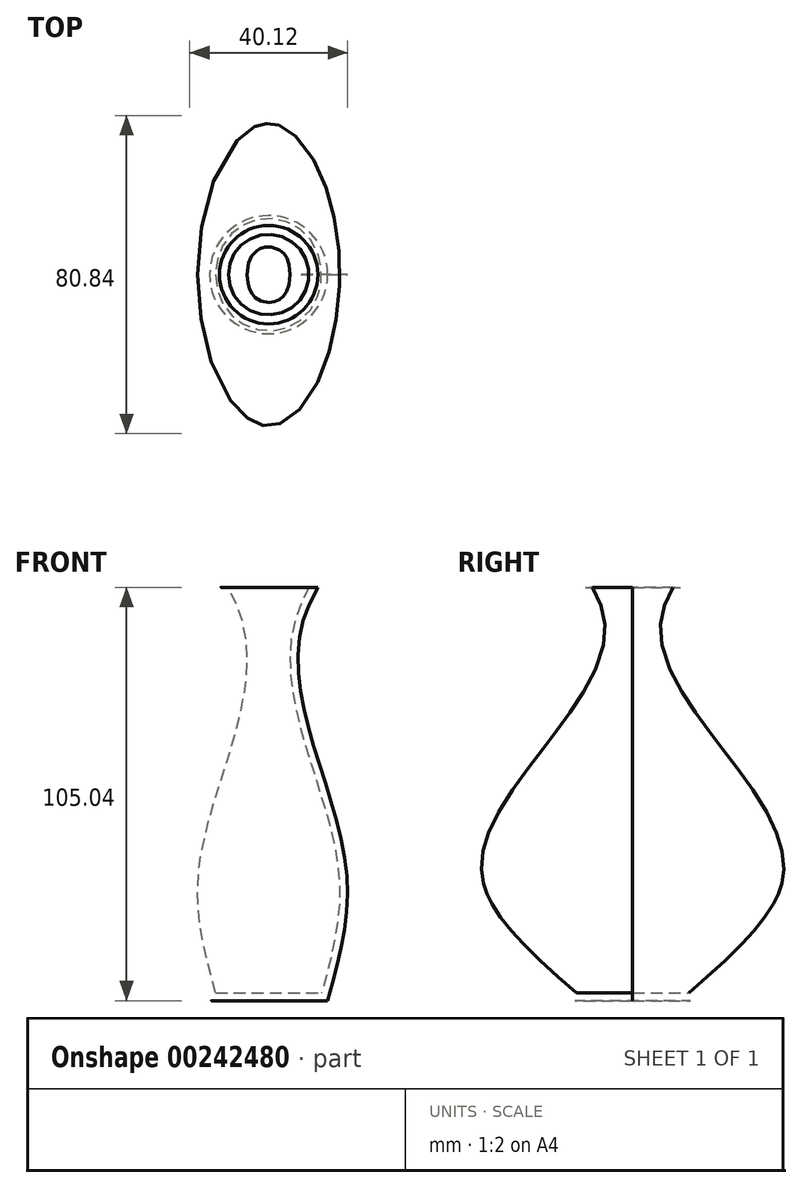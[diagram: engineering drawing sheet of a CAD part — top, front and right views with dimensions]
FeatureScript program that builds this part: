
annotation { "Feature Type Name" : "Feature", "Feature Type Description" : "" }
export const myFeature = defineFeature(function(context is Context, id is Id, definition is map)
    precondition{}
    {
        {
            var Q0;
            Q0=qCreatedBy(makeId("Top.planeOp"),FACE);
            var sketch = newSketch(context, id + "F0", { "sketchPlane" : qUnion([Q0])});
            skCircle(sketch, "E0", {"center": v(0, 0) * mm, "radius": 15 * mm});
            skSolve(sketch);
        }
        {
            var Q0;
            Q0=qCreatedBy(makeId("Top.planeOp"),FACE);
            cPlane(context, id + "F1", {"entities" : qUnion([Q0]), "cplaneType" : CPlaneType.OFFSET, "offset" : 30 * mm, "width" : 150 * mm, "height" : 150 * mm});
        }
        {
            var Q0;
            Q0=qCreatedBy(id+"F1.planeOp",FACE);
            var sketch = newSketch(context, id + "F2", { "sketchPlane" : qUnion([Q0])});
            skEllipse(sketch, "E1", {"center": v(0, 0) * mm, "majorRadius": 40 * mm, "minorRadius": 20 * mm, "majorAxis": v(0, -1)});
            skSolve(sketch);
        }
        {
            var Q0;
            Q0=qCreatedBy(makeId("Top.planeOp"),FACE);
            cPlane(context, id + "F3", {"entities" : qUnion([Q0]), "cplaneType" : CPlaneType.OFFSET, "offset" : 100 * mm, "width" : 150 * mm, "height" : 150 * mm});
        }
        {
            var Q0;
            Q0=qCreatedBy(id+"F3.planeOp",FACE);
            var sketch = newSketch(context, id + "F4", { "sketchPlane" : qUnion([Q0])});
            skCircle(sketch, "E2", {"center": v(0, 0) * mm, "radius": 10 * mm});
            skSolve(sketch);
        }
        {
            var Q0;
            Q0=qCreatedBy(makeId("Top.planeOp"),FACE);
            cPlane(context, id + "F5", {"entities" : qUnion([Q0]), "cplaneType" : CPlaneType.OFFSET, "offset" : 105 * mm, "width" : 150 * mm, "height" : 150 * mm});
        }
        {
            var Q0;
            Q0=qCreatedBy(id+"F5.planeOp",FACE);
            var sketch = newSketch(context, id + "F6", { "sketchPlane" : qUnion([Q0])});
            skCircle(sketch, "E3", {"center": v(0, 0) * mm, "radius": 12.5 * mm});
            skSolve(sketch);
        }
        {
            var Q0;
            Q0=makeQuery(id+"F0.imprint","IMPRINT",FACE,{"disambiguationData":[TD([[makeQuery(id+"F0.imprint","IMPRINT",EDGE,{"derivedFrom":sQuery(id+"F0.wireOp",EDGE,"E0")}),1.0]])]});
            var Q1;
            Q1=makeQuery(id+"F2.imprint","IMPRINT",FACE,{"disambiguationData":[TD([[makeQuery(id+"F2.imprint","IMPRINT",EDGE,{"derivedFrom":sQuery(id+"F2.wireOp",EDGE,"E1")}),1.0]])]});
            var Q2;
            Q2=makeQuery(id+"F4.imprint","IMPRINT",FACE,{"disambiguationData":[TD([[makeQuery(id+"F4.imprint","IMPRINT",EDGE,{"derivedFrom":sQuery(id+"F4.wireOp",EDGE,"E2")}),1.0]])]});
            var Q3;
            Q3=makeQuery(id+"F6.imprint","IMPRINT",FACE,{"disambiguationData":[TD([[makeQuery(id+"F6.imprint","IMPRINT",EDGE,{"derivedFrom":sQuery(id+"F6.wireOp",EDGE,"E3")}),1.0]])]});
            loft(context, id + "F7", {"sheetProfilesArray" : [{ "sheetProfileEntities" : qUnion([Q0]) }, { "sheetProfileEntities" : qUnion([Q1]) }, { "sheetProfileEntities" : qUnion([Q2]) }, { "sheetProfileEntities" : qUnion([Q3]) }]});
        }
        {
            var Q0;
            Q0=makeQuery(id+"F7.opLoft","CAP_FACE",FACE,{"disambiguationData":[OSD([makeQuery(id+"F6.imprint","IMPRINT",FACE,{"disambiguationData":[TD([[makeQuery(id+"F6.imprint","IMPRINT",EDGE,{"derivedFrom":sQuery(id+"F6.wireOp",EDGE,"E3")}),1.0]])]})])],"isStart":true});
            shell(context, id + "F8", {"entities" : qUnion([Q0]), "thickness" : 2 * mm});
        }
    });
